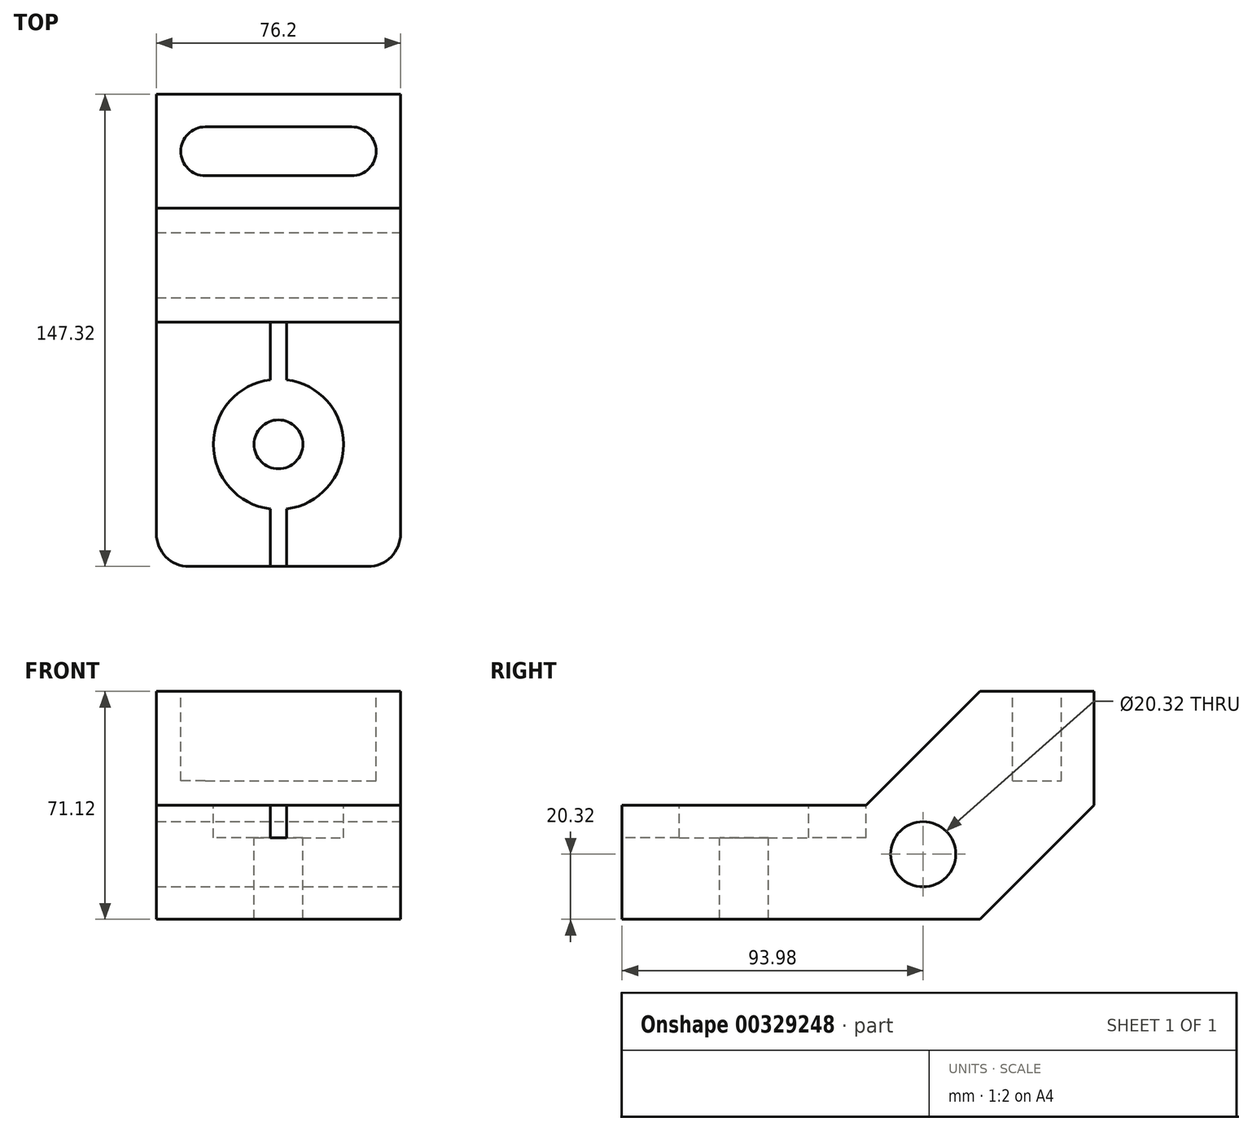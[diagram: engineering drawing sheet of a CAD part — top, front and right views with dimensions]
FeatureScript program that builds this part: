
annotation { "Feature Type Name" : "Feature", "Feature Type Description" : "" }
export const myFeature = defineFeature(function(context is Context, id is Id, definition is map)
    precondition{}
    {
        {
            var Q0;
            Q0=qCreatedBy(makeId("Right.planeOp"),FACE);
            var sketch = newSketch(context, id + "F0", { "sketchPlane" : qUnion([Q0])});
            skLineSegment(sketch, "E0", {"start": v(0, 0) * mm, "end": v(0, 35.56) * mm});
            skLineSegment(sketch, "E1", {"start": v(0, 35.56) * mm, "end": v(76.2, 35.56) * mm});
            skLineSegment(sketch, "E2", {"start": v(76.2, 35.56) * mm, "end": v(111.76, 71.12) * mm});
            skLineSegment(sketch, "E3", {"start": v(111.76, 71.12) * mm, "end": v(147.32, 71.12) * mm});
            skLineSegment(sketch, "E4", {"start": v(147.32, 71.12) * mm, "end": v(147.32, 35.56) * mm});
            skLineSegment(sketch, "E5", {"start": v(147.32, 35.56) * mm, "end": v(111.76, 0) * mm});
            skLineSegment(sketch, "E6", {"start": v(111.76, 0) * mm, "end": v(0, 0) * mm});
            skSolve(sketch);
        }
        {
            var Q0;
            Q0 = qSketchRegion(id + "F0", true);
            extrude(context, id + "F1", {"entities" : qUnion([Q0]), "endBound" : BoundingType.SYMMETRIC, "depth" : 76.2 * mm});
        }
        {
            var Q0;
            Q0=makeQuery(id+"F1.opExtrude","SWEPT_FACE",FACE,{"disambiguationData":[OSD([sQuery(id+"F0.wireOp",EDGE,"E3")])]});
            var sketch = newSketch(context, id + "F2", { "sketchPlane" : qUnion([Q0])});
            skLineSegment(sketch, "E7", {"start": v(-22.86, 137.16) * mm, "end": v(22.86, 137.16) * mm});
            skLineSegment(sketch, "E8", {"start": v(-22.86, 121.92) * mm, "end": v(22.86, 121.92) * mm});
            skArc(sketch, "E9", {"start": v(22.86, 137.16) * mm, "mid": v(30.48, 129.54) * mm, "end": v(22.86, 121.92) * mm});
            skArc(sketch, "E10", {"start": v(-22.86, 137.16) * mm, "mid": v(-30.48, 129.54) * mm, "end": v(-22.86, 121.92) * mm});
            skSolve(sketch);
        }
        {
            var Q0;
            Q0=makeQuery(id+"F2.imprint","IMPRINT",FACE,{"disambiguationData":[TD([[makeQuery(id+"F2.imprint","IMPRINT",EDGE,{"derivedFrom":sQuery(id+"F2.wireOp",EDGE,"E7")}),-1.0]])]});
            extrude(context, id + "F3", {"entities" : qUnion([Q0]), "operationType" : NewBodyOperationType.REMOVE, "oppositeDirection" : true, "depth" : 27.94 * mm});
        }
        {
            var Q0;
            Q0=makeQuery(id+"F1.opExtrude","CAP_EDGE",EDGE,{"disambiguationData":[OSD([sQuery(id+"F0.wireOp",EDGE,"E0")])],"isStart":false});
            var Q1;
            Q1=makeQuery(id+"F1.opExtrude","CAP_EDGE",EDGE,{"disambiguationData":[OSD([sQuery(id+"F0.wireOp",EDGE,"E0")])],"isStart":true});
            fillet(context, id + "F4", {"entities" : qUnion([Q0, Q1]), "radius" : 10.16 * mm, "tangentPropagation" : true, "allowEdgeOverflow" : false});
        }
        {
            var Q0;
            Q0=makeQuery(id+"F1.opExtrude","CAP_FACE",FACE,{"disambiguationData":[OSD([sQuery(id+"F0.wireOp",EDGE,"E0"),sQuery(id+"F0.wireOp",EDGE,"E1"),sQuery(id+"F0.wireOp",EDGE,"E2"),sQuery(id+"F0.wireOp",EDGE,"E3"),sQuery(id+"F0.wireOp",EDGE,"E4"),sQuery(id+"F0.wireOp",EDGE,"E5"),sQuery(id+"F0.wireOp",EDGE,"E6")])],"isStart":false});
            var sketch = newSketch(context, id + "F5", { "sketchPlane" : qUnion([Q0])});
            skCircle(sketch, "E11", {"center": v(93.98, 20.32) * mm, "radius": 10.16 * mm});
            skSolve(sketch);
        }
        {
            var Q0;
            Q0 = qSketchRegion(id + "F5", true);
            extrude(context, id + "F6", {"entities" : qUnion([Q0]), "operationType" : NewBodyOperationType.REMOVE, "endBound" : BoundingType.THROUGH_ALL, "oppositeDirection" : true, "depth" : 25.4 * mm});
        }
        {
            var Q0;
            Q0=makeQuery(id+"F1.opExtrude","SWEPT_FACE",FACE,{"disambiguationData":[OSD([sQuery(id+"F0.wireOp",EDGE,"E1")])]});
            var sketch = newSketch(context, id + "F7", { "sketchPlane" : qUnion([Q0])});
            skCircle(sketch, "E12", {"center": v(0, 38.1) * mm, "radius": 7.62 * mm});
            skLineSegment(sketch, "E13.bottom", {"start": v(-2.54, 76.2) * mm, "end": v(2.54, 76.2) * mm});
            skLineSegment(sketch, "E13.top", {"start": v(-2.54, 0) * mm, "end": v(2.54, 0) * mm});
            skLineSegment(sketch, "E13.left", {"start": v(-2.54, 76.2) * mm, "end": v(-2.54, 0) * mm});
            skLineSegment(sketch, "E13.right", {"start": v(2.54, 76.2) * mm, "end": v(2.54, 0) * mm});
            skSolve(sketch);
        }
        {
            var Q0;
            Q0=sQuery(id+"F7.wireOp",VERTEX,"E12.center");
            var Q1;
            Q1=makeQuery(id+"F1.opExtrude","SWEPT_BODY",BODY,{"disambiguationData":[OSD([sQuery(id+"F0.wireOp",EDGE,"E0"),sQuery(id+"F0.wireOp",EDGE,"E1"),sQuery(id+"F0.wireOp",EDGE,"E2"),sQuery(id+"F0.wireOp",EDGE,"E3"),sQuery(id+"F0.wireOp",EDGE,"E4"),sQuery(id+"F0.wireOp",EDGE,"E5"),sQuery(id+"F0.wireOp",EDGE,"E6")])]});
            hole(context, id + "F8", {"style" : HoleStyle.C_BORE, "endStyle" : HoleEndStyle.THROUGH, "holeDiameter" : 15.24 * mm, "cBoreDiameter" : 40.64 * mm, "cBoreDepth" : 10.16 * mm, "tappedDepth" : 12.7 * mm, "tapClearance" : 3, "locations" : qUnion([Q0]), "scope" : qUnion([Q1])});
        }
        {
            var Q0;
            {var subQ5=sQuery(id+"F7.wireOp",EDGE,"E13.top");Q0=makeQuery(id+"F7.imprint","IMPRINT",FACE,{"disambiguationData":[TD([[makeQuery(id+"F7.imprint","IMPRINT",EDGE,{"derivedFrom":subQ5}),-1.0]])]});}
            var Q1;
            {var subQ5=sQuery(id+"F7.wireOp",EDGE,"E13.bottom");Q1=makeQuery(id+"F7.imprint","IMPRINT",FACE,{"disambiguationData":[TD([[makeQuery(id+"F7.imprint","IMPRINT",EDGE,{"derivedFrom":subQ5}),1.0]])]});}
            extrude(context, id + "F9", {"entities" : qUnion([Q0, Q1]), "operationType" : NewBodyOperationType.REMOVE, "oppositeDirection" : true, "depth" : 10.16 * mm});
        }
    });
